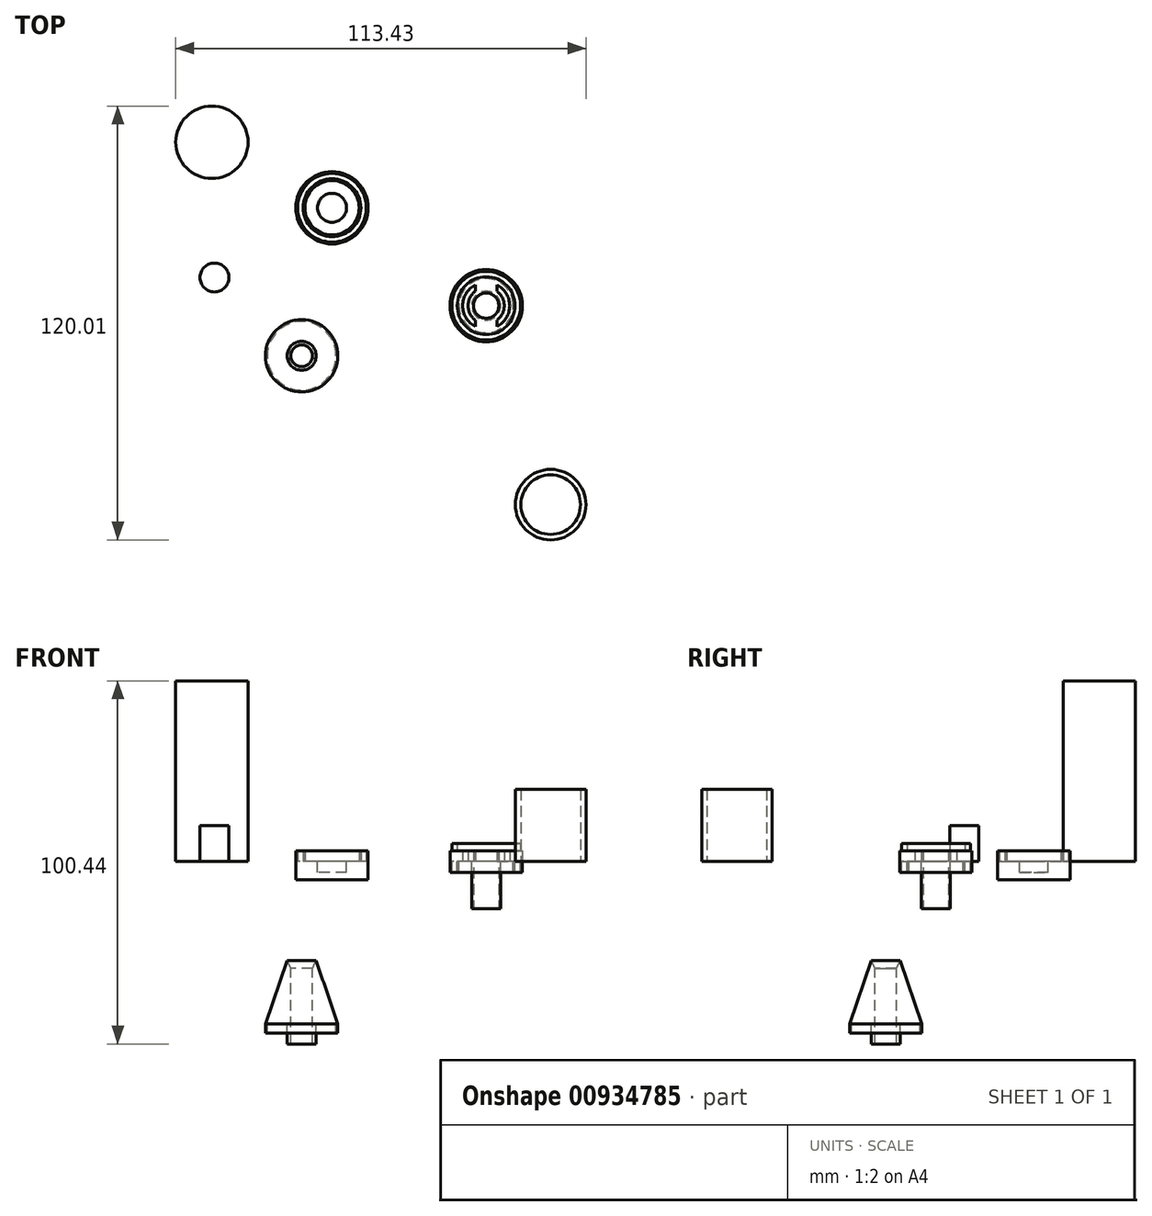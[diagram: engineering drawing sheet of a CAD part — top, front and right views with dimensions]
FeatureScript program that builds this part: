
annotation { "Feature Type Name" : "Feature", "Feature Type Description" : "" }
export const myFeature = defineFeature(function(context is Context, id is Id, definition is map)
    precondition{}
    {
        {
            var Q0;
            Q0=qCreatedBy(makeId("Top.planeOp"),FACE);
            var sketch = newSketch(context, id + "F0", { "sketchPlane" : qUnion([Q0])});
            skCircle(sketch, "E0", {"center": v(-58.68, 59.07) * mm, "radius": 10 * mm});
            skSolve(sketch);
        }
        {
            var Q0;
            Q0=makeQuery(id+"F0.imprint","IMPRINT",FACE,{"disambiguationData":[TD([[makeQuery(id+"F0.imprint","IMPRINT",EDGE,{"derivedFrom":sQuery(id+"F0.wireOp",EDGE,"E0")}),1.0]])]});
            extrude(context, id + "F1", {"entities" : qUnion([Q0]), "depth" : 50 * mm, "offsetDistance" : 25 * mm});
        }
        {
            var Q0;
            Q0=qCreatedBy(makeId("Top.planeOp"),FACE);
            var sketch = newSketch(context, id + "F2", { "sketchPlane" : qUnion([Q0])});
            skCircle(sketch, "E1", {"center": v(-25.47, 40.94) * mm, "radius": 10 * mm});
            skCircle(sketch, "E2.0", {"center": v(-25.47, 40.94) * mm, "radius": 9.5 * mm});
            skCircle(sketch, "E3.0", {"center": v(-25.47, 40.94) * mm, "radius": 8 * mm});
            skCircle(sketch, "E4.0", {"center": v(-25.47, 40.94) * mm, "radius": 7.5 * mm});
            skCircle(sketch, "E5", {"center": v(-25.47, 40.94) * mm, "radius": 4 * mm});
            skSolve(sketch);
        }
        {
            var Q0;
            Q0=makeQuery(id+"F2.imprint","IMPRINT",FACE,{"disambiguationData":[TD([[makeQuery(id+"F2.imprint","IMPRINT",EDGE,{"derivedFrom":sQuery(id+"F2.wireOp",EDGE,"E2.0")}),1.0]])]});
            var Q1;
            Q1=makeQuery(id+"F2.imprint","IMPRINT",FACE,{"disambiguationData":[TD([[makeQuery(id+"F2.imprint","IMPRINT",EDGE,{"derivedFrom":sQuery(id+"F2.wireOp",EDGE,"E3.0")}),1.0]])]});
            var Q2;
            Q2=makeQuery(id+"F2.imprint","IMPRINT",FACE,{"disambiguationData":[TD([[makeQuery(id+"F2.imprint","IMPRINT",EDGE,{"derivedFrom":sQuery(id+"F2.wireOp",EDGE,"E4.0")}),1.0]])]});
            var Q3;
            Q3=makeQuery(id+"F2.imprint","IMPRINT",FACE,{"disambiguationData":[TD([[makeQuery(id+"F2.imprint","IMPRINT",EDGE,{"derivedFrom":sQuery(id+"F2.wireOp",EDGE,"E1")}),1.0]])]});
            var Q4;
            Q4=makeQuery(id+"F2.imprint","IMPRINT",FACE,{"disambiguationData":[TD([[makeQuery(id+"F2.imprint","IMPRINT",EDGE,{"derivedFrom":sQuery(id+"F2.wireOp",EDGE,"E5")}),1.0]])]});
            extrude(context, id + "F3", {"entities" : qUnion([Q0, Q1, Q2, Q3, Q4]), "oppositeDirection" : true, "depth" : 5 * mm, "offsetDistance" : 25 * mm});
        }
        {
            var Q0;
            Q0=makeQuery(id+"F2.imprint","IMPRINT",FACE,{"disambiguationData":[TD([[makeQuery(id+"F2.imprint","IMPRINT",EDGE,{"derivedFrom":sQuery(id+"F2.wireOp",EDGE,"E1")}),1.0]])]});
            var Q1;
            Q1=makeQuery(id+"F2.imprint","IMPRINT",FACE,{"disambiguationData":[TD([[makeQuery(id+"F2.imprint","IMPRINT",EDGE,{"derivedFrom":sQuery(id+"F2.wireOp",EDGE,"E3.0")}),1.0]])]});
            extrude(context, id + "F4", {"entities" : qUnion([Q0, Q1]), "operationType" : NewBodyOperationType.ADD, "depth" : 3 * mm, "offsetDistance" : 25 * mm});
        }
        {
            var Q0;
            Q0=makeQuery(id+"F2.imprint","IMPRINT",FACE,{"disambiguationData":[TD([[makeQuery(id+"F2.imprint","IMPRINT",EDGE,{"derivedFrom":sQuery(id+"F2.wireOp",EDGE,"E5")}),1.0]])]});
            extrude(context, id + "F5", {"entities" : qUnion([Q0]), "operationType" : NewBodyOperationType.REMOVE, "oppositeDirection" : true, "depth" : 3 * mm, "offsetDistance" : 25 * mm});
        }
        {
            var Q0;
            Q0=qCreatedBy(makeId("Top.planeOp"),FACE);
            var sketch = newSketch(context, id + "F6", { "sketchPlane" : qUnion([Q0])});
            skCircle(sketch, "E6", {"center": v(-57.98, 21.65) * mm, "radius": 4 * mm});
            skSolve(sketch);
        }
        {
            var Q0;
            Q0=makeQuery(id+"F6.imprint","IMPRINT",FACE,{"disambiguationData":[TD([[makeQuery(id+"F6.imprint","IMPRINT",EDGE,{"derivedFrom":sQuery(id+"F6.wireOp",EDGE,"E6")}),1.0]])]});
            extrude(context, id + "F7", {"entities" : qUnion([Q0]), "depth" : 10 * mm, "offsetDistance" : 25 * mm});
        }
        {
            var Q0;
            Q0=qCreatedBy(makeId("Top.planeOp"),FACE);
            var sketch = newSketch(context, id + "F8", { "sketchPlane" : qUnion([Q0])});
            skCircle(sketch, "E7", {"center": v(17.16, 13.85) * mm, "radius": 10 * mm});
            skCircle(sketch, "E8.0", {"center": v(17.16, 13.85) * mm, "radius": 9.5 * mm});
            skCircle(sketch, "E9.0", {"center": v(17.16, 13.85) * mm, "radius": 8 * mm});
            skCircle(sketch, "E10.0", {"center": v(17.16, 13.85) * mm, "radius": 7.5 * mm});
            skCircle(sketch, "E11", {"center": v(17.16, 13.85) * mm, "radius": 4 * mm});
            skCircle(sketch, "E12.0", {"center": v(17.16, 13.85) * mm, "radius": 3.5 * mm});
            skArc(sketch, "E13.0", {"start": v(14.16, 19.62) * mm, "mid": v(10.66, 13.85) * mm, "end": v(14.16, 8.08) * mm});
            skArc(sketch, "E14.0", {"start": v(14.16, 17.85) * mm, "mid": v(12.16, 13.85) * mm, "end": v(14.16, 9.85) * mm});
            skLineSegment(sketch, "E15.0", {"start": v(14.16, 9.85) * mm, "end": v(14.16, 8.08) * mm});
            skLineSegment(sketch, "E16.0", {"start": v(20.16, 9.85) * mm, "end": v(20.16, 8.08) * mm});
            skLineSegment(sketch, "E17.0", {"start": v(20.16, 17.85) * mm, "end": v(20.16, 19.62) * mm});
            skLineSegment(sketch, "E18.0", {"start": v(14.16, 17.85) * mm, "end": v(14.16, 19.62) * mm});
            skArc(sketch, "E19.trimOffspring", {"start": v(20.16, 9.85) * mm, "mid": v(22.16, 13.85) * mm, "end": v(20.16, 17.85) * mm});
            skArc(sketch, "E20.trimOffspring", {"start": v(20.16, 8.08) * mm, "mid": v(23.66, 13.85) * mm, "end": v(20.16, 19.62) * mm});
            skSolve(sketch);
        }
        {
            var Q0;
            Q0=makeQuery(id+"F8.imprint","IMPRINT",FACE,{"disambiguationData":[TD([[makeQuery(id+"F8.imprint","IMPRINT",EDGE,{"derivedFrom":sQuery(id+"F8.wireOp",EDGE,"E10.0")}),1.0]])]});
            var Q1;
            Q1=makeQuery(id+"F8.imprint","IMPRINT",FACE,{"disambiguationData":[TD([[makeQuery(id+"F8.imprint","IMPRINT",EDGE,{"derivedFrom":sQuery(id+"F8.wireOp",EDGE,"E11")}),1.0]])]});
            var Q2;
            Q2=makeQuery(id+"F8.imprint","IMPRINT",FACE,{"disambiguationData":[TD([[makeQuery(id+"F8.imprint","IMPRINT",EDGE,{"derivedFrom":sQuery(id+"F8.wireOp",EDGE,"E9.0")}),1.0]])]});
            var Q3;
            Q3=makeQuery(id+"F8.imprint","IMPRINT",FACE,{"disambiguationData":[TD([[makeQuery(id+"F8.imprint","IMPRINT",EDGE,{"derivedFrom":sQuery(id+"F8.wireOp",EDGE,"E8.0")}),1.0]])]});
            var Q4;
            Q4=makeQuery(id+"F8.imprint","IMPRINT",FACE,{"disambiguationData":[TD([[makeQuery(id+"F8.imprint","IMPRINT",EDGE,{"derivedFrom":sQuery(id+"F8.wireOp",EDGE,"E7")}),1.0]])]});
            extrude(context, id + "F9", {"entities" : qUnion([Q0, Q1, Q2, Q3, Q4]), "depth" : 3 * mm, "offsetDistance" : 25 * mm});
        }
        {
            var Q0;
            Q0=makeQuery(id+"F8.imprint","IMPRINT",FACE,{"disambiguationData":[TD([[makeQuery(id+"F8.imprint","IMPRINT",EDGE,{"derivedFrom":sQuery(id+"F8.wireOp",EDGE,"E7")}),1.0]])]});
            var Q1;
            Q1=makeQuery(id+"F8.imprint","IMPRINT",FACE,{"disambiguationData":[TD([[makeQuery(id+"F8.imprint","IMPRINT",EDGE,{"derivedFrom":sQuery(id+"F8.wireOp",EDGE,"E9.0")}),1.0]])]});
            extrude(context, id + "F10", {"entities" : qUnion([Q0, Q1]), "operationType" : NewBodyOperationType.ADD, "oppositeDirection" : true, "depth" : 3 * mm, "offsetDistance" : 25 * mm});
        }
        {
            var Q0;
            Q0=makeQuery(id+"F8.imprint","IMPRINT",FACE,{"disambiguationData":[TD([[makeQuery(id+"F8.imprint","IMPRINT",EDGE,{"derivedFrom":sQuery(id+"F8.wireOp",EDGE,"E11")}),1.0]])]});
            extrude(context, id + "F11", {"entities" : qUnion([Q0]), "operationType" : NewBodyOperationType.ADD, "oppositeDirection" : true, "depth" : 13 * mm, "offsetDistance" : 25 * mm});
        }
        {
            var Q0;
            Q0=makeQuery(id+"F8.imprint","IMPRINT",FACE,{"disambiguationData":[TD([[makeQuery(id+"F8.imprint","IMPRINT",EDGE,{"derivedFrom":sQuery(id+"F8.wireOp",EDGE,"E8.0")}),1.0]])]});
            extrude(context, id + "F12", {"entities" : qUnion([Q0]), "operationType" : NewBodyOperationType.ADD, "depth" : 5 * mm, "offsetDistance" : 25 * mm});
        }
        {
            var Q0;
            Q0=qCreatedBy(makeId("Front.planeOp"),FACE);
            var sketch = newSketch(context, id + "F13", { "sketchPlane" : qUnion([Q0])});
            skLineSegment(sketch, "E21.top", {"start": v(-43.85, -47.44) * mm, "end": v(-43.35, -47.44) * mm});
            skLineSegment(sketch, "E21.left", {"start": v(-43.85, -44.94) * mm, "end": v(-43.85, -47.44) * mm});
            skLineSegment(sketch, "E21.right", {"start": v(-33.85, -27.44) * mm, "end": v(-33.85, -47.44) * mm});
            skLineSegment(sketch, "E22", {"start": v(-43.35, -47.44) * mm, "end": v(-43.35, -44.94) * mm});
            skLineSegment(sketch, "E23", {"start": v(-37.85, -47.44) * mm, "end": v(-37.85, -50.44) * mm});
            skLineSegment(sketch, "E24", {"start": v(-36.85, -47.44) * mm, "end": v(-36.85, -50.44) * mm});
            skLineSegment(sketch, "E25", {"start": v(-36.85, -50.44) * mm, "end": v(-37.85, -50.44) * mm});
            skLineSegment(sketch, "E26", {"start": v(-37.85, -47.44) * mm, "end": v(-37.85, -44.94) * mm});
            skLineSegment(sketch, "E27", {"start": v(-36.85, -47.44) * mm, "end": v(-36.85, -29.5) * mm});
            skLineSegment(sketch, "E28", {"start": v(-43.35, -44.94) * mm, "end": v(-37.85, -44.94) * mm});
            skLineSegment(sketch, "E29", {"start": v(-43.85, -44.94) * mm, "end": v(-37.85, -27.44) * mm});
            skLineSegment(sketch, "E30", {"start": v(-37.85, -27.44) * mm, "end": v(-36.85, -29.5) * mm});
            skSolve(sketch);
        }
        {
            var Q0;
            Q0=makeQuery(id+"F13.imprint","IMPRINT",FACE,{"disambiguationData":[TD([[makeQuery(id+"F13.imprint","IMPRINT",EDGE,{"derivedFrom":sQuery(id+"F13.wireOp",EDGE,"E21.left")}),1.0]])]});
            var Q1;
            Q1=sQuery(id+"F13.wireOp",EDGE,"E21.right");
            revolve(context, id + "F14", {"surfaceOperationType" : NewSurfaceOperationType.NEW, "entities" : qUnion([Q0]), "axis" : qUnion([Q1]), "revolveType" : RevolveType.FULL});
        }
        {
            var Q0;
            Q0=qCreatedBy(makeId("Top.planeOp"),FACE);
            var sketch = newSketch(context, id + "F15", { "sketchPlane" : qUnion([Q0])});
            skCircle(sketch, "E31", {"center": v(35, -41.19) * mm, "radius": 9.75 * mm});
            skCircle(sketch, "E32.0", {"center": v(35, -41.19) * mm, "radius": 8.25 * mm});
            skSolve(sketch);
        }
        {
            var Q0;
            Q0=makeQuery(id+"F15.imprint","IMPRINT",FACE,{"disambiguationData":[TD([[makeQuery(id+"F15.imprint","IMPRINT",EDGE,{"derivedFrom":sQuery(id+"F15.wireOp",EDGE,"E31")}),1.0]])]});
            extrude(context, id + "F16", {"entities" : qUnion([Q0]), "depth" : 20 * mm, "offsetDistance" : 25 * mm});
        }
    });
